# Revit family: Papelera Kube Selectif
name_source: partatom
category: Furniture
units: mm (PartAtom-declared; Revit-internal decimal feet)

## family parameters
Always vertical = Yes
Cut with Voids When Loaded = No
OmniClass Number = 23.40.20.00
OmniClass Title = General Furniture and Specialties
Room Calculation Point = No
Shared = No
Work Plane-Based = No

## types (6) — shared parameters
Material = <By Category>
zero-valued in all types: Default Elevation

## per-type parameters (varying)
| type | A | B | H | Papelera Kube Selctif | Papelera Kube Selectif-PA672S2 | Papelera Kube Selectif-PA672S3 | Top Cover |
| Papelera Kube Selectif-PA672SV-510mm | 0.51 m | 0.51 m | 1.1 m | Yes | No | No | Steel PA672SV |
| Papelera Kube Selectif-PA672SM-510mm | 0 m | 0 m | 0 m | Yes | No | No | Steel PA672SM |
| Papelera Kube Selectif-PA672SAZ-510mm | 0 m | 0 m | 0 m | Yes | No | No | Steel PA672SAZ |
| Papelera Kube Selectif-PA672SA-510mm | 0 m | 0 m | 0 m | Yes | No | No | Steel PA672SA |
| Papelera Kube Selectif-PA672S2-510mm | 0 m | 0 m | 0 m | No | Yes | No | Steel PA672SAZ |
| Papelera Kube Selectif-PA672S3-510mm | 0 m | 0 m | 0 m | No | No | Yes | Steel PA672SAZ |

## geometry (parser evidence)
native form markers: Blend x4, Sweep x11
no freeform markers — native parametric forms only
